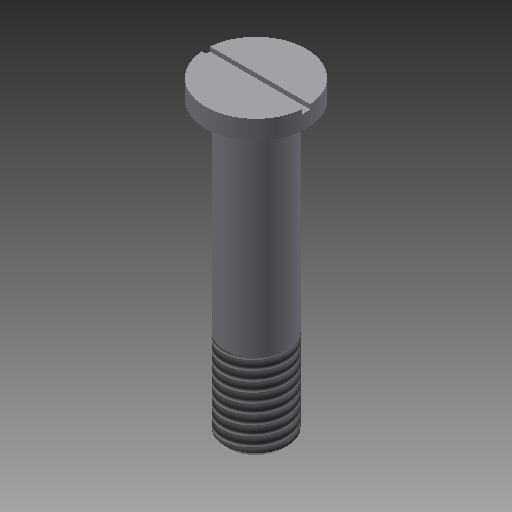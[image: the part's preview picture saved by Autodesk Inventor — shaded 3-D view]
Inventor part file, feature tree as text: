
AUTODESK INVENTOR PART (.ipt)
format: ipt  version: 2018 (Build 220112000, 112)  size: 122,880 bytes
history: native  units: mm
features: other x7, sketch x3, extrude x2, revolve x1, thread x1
ambient origin geometry x8: Origin, YZ Plane, XZ Plane, XY Plane, X Axis, Y Axis, Z Axis, Center Point
bodies: Solid1 (feature_tree)
feature tree (14):
  extrude  "Extrusion1"  Depth=1.3mm TaperAngle=0.0deg
  extrude  "Extrusion2"  Depth=14.0mm
  revolve  "Revolution1"  [1 undecoded]
  thread  "Thread1"  [1 undecoded]
  other  "hebel_XY"
  other  "hebel_YZ"
  other  "hebel_ZX"
  other  "hebel_X"
  other  "hebel_Y"
  other  "hebel_Z"
  other  "hebel_Center"
  sketch  "Skizze_1"  dims[d0=3.0mm d1=0.0mm d2=1.3mm d3=0.0mm]
  sketch  "Skizze_3"
  sketch  "Skizze_2"  dims[d4=360.0deg d5=14.0mm d6=32.0mm]
note: 2 required parameter values undecoded (feature->parameter linkage not recoverable at this tier; creation-order binding heuristic only, values carry confidence <= 0.55)
